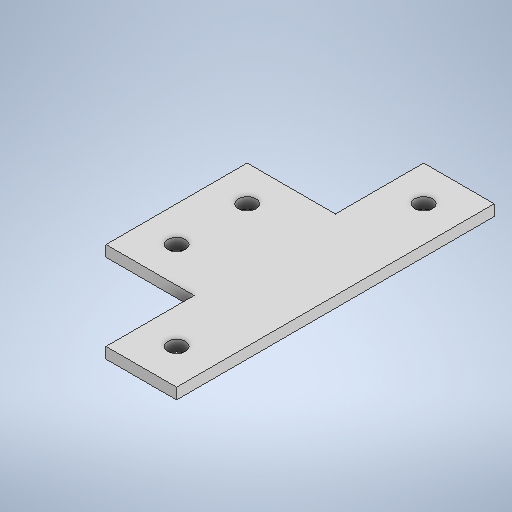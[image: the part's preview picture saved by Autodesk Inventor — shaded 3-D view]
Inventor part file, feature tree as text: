
AUTODESK INVENTOR PART (.ipt)
format: ipt  version: 2025.1 (Build 291241000, 241)  size: 247,296 bytes
history: native  units: in
note: dims shown in document units (in); Inventor stores cm internally (conversion verified against a paired STEP export)
features: extrude x1, sketch x1
ambient origin geometry x8: Origin, YZ Plane, XZ Plane, XY Plane, X Axis, Y Axis, Z Axis, Center Point
bodies: Solid1 (feature_tree)
feature tree (2):
  extrude  "Extrusion1"  Depth=1.6in
  sketch  "Sketch1"  dims[d0=1.0in d1=1.6in d2=0.4in d3=0.4in d4=90.0deg d5=0.4in d6=0.4in d7=90.0deg d8=0.2in d9=0.2in d10=1.0in d11=90.0deg d12=0.8in d13=3.6in d14=90.0deg d15=0.8in d16=90.0deg d17=0.4in d18=90.0deg d19=0.4in d20=90.0deg d21=0.2in d22=0.2in d23=0.125in d24=0.0in]
